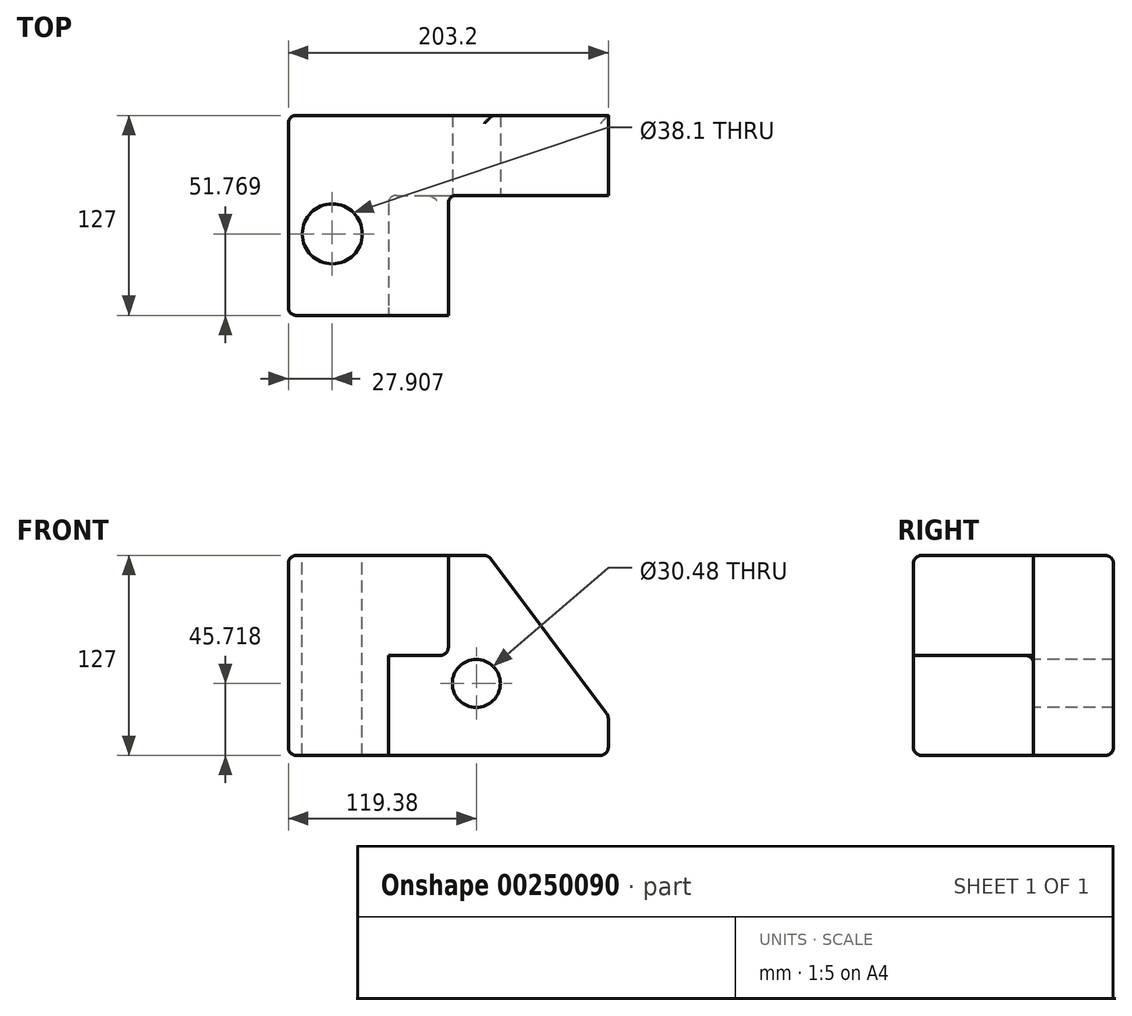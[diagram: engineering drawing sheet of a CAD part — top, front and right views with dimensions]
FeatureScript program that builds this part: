
annotation { "Feature Type Name" : "Feature", "Feature Type Description" : "" }
export const myFeature = defineFeature(function(context is Context, id is Id, definition is map)
    precondition{}
    {
        {
            var Q0;
            Q0=qCreatedBy(makeId("Front.planeOp"),FACE);
            var sketch = newSketch(context, id + "F0", { "sketchPlane" : qUnion([Q0])});
            skLineSegment(sketch, "E0.bottom", {"start": v(-90.02, 64.6) * mm, "end": v(113.18, 64.6) * mm});
            skLineSegment(sketch, "E0.top", {"start": v(-90.02, -62.4) * mm, "end": v(113.18, -62.4) * mm});
            skLineSegment(sketch, "E0.left", {"start": v(-90.02, 64.6) * mm, "end": v(-90.02, -62.4) * mm});
            skLineSegment(sketch, "E0.right", {"start": v(113.18, 64.6) * mm, "end": v(113.18, -62.4) * mm});
            skSolve(sketch);
        }
        {
            var Q0;
            Q0 = qSketchRegion(id + "F0", true);
            extrude(context, id + "F1", {"entities" : qUnion([Q0]), "depth" : 127 * mm});
        }
        {
            var Q0;
            Q0=makeQuery(id+"F1.opExtrude","CAP_FACE",FACE,{"disambiguationData":[OSD([sQuery(id+"F0.wireOp",EDGE,"E0.bottom"),sQuery(id+"F0.wireOp",EDGE,"E0.top"),sQuery(id+"F0.wireOp",EDGE,"E0.left"),sQuery(id+"F0.wireOp",EDGE,"E0.right")])],"isStart":false});
            var sketch = newSketch(context, id + "F2", { "sketchPlane" : qUnion([Q0])});
            skLineSegment(sketch, "E1.top", {"start": v(-90.02, -62.4) * mm, "end": v(-26.52, -62.4) * mm});
            skLineSegment(sketch, "E1.left", {"start": v(-90.02, 64.6) * mm, "end": v(-90.02, -62.4) * mm});
            skLineSegment(sketch, "E1.right", {"start": v(-26.52, 1.1) * mm, "end": v(-26.52, -62.4) * mm});
            skLineSegment(sketch, "E2", {"start": v(-26.52, 1.1) * mm, "end": v(11.58, 1.1) * mm});
            skLineSegment(sketch, "E3", {"start": v(11.58, 1.1) * mm, "end": v(11.58, 64.6) * mm});
            skLineSegment(sketch, "E4", {"start": v(-90.02, 64.6) * mm, "end": v(11.58, 64.6) * mm});
            skSolve(sketch);
        }
        {
            var Q0;
            {var subQ3=sQuery(id+"F2.wireOp",EDGE,"E1.right");Q0=makeQuery(id+"F2.imprint","IMPRINT",FACE,{"disambiguationData":[TD([[makeQuery(id+"F2.imprint","IMPRINT",EDGE,{"derivedFrom":subQ3}),1.0]])]});}
            extrude(context, id + "F3", {"entities" : qUnion([Q0]), "operationType" : NewBodyOperationType.REMOVE, "oppositeDirection" : true, "depth" : 76.2 * mm});
        }
        {
            var Q0;
            Q0=makeQuery(id+"F1.opExtrude","SWEPT_EDGE",EDGE,{"disambiguationData":[OSD([sQuery(id+"F0.wireOp",EDGE,"E0.bottom"),sQuery(id+"F0.wireOp",EDGE,"E0.right")])]});
            chamfer(context, id + "F4", {"entities" : qUnion([Q0]), "chamferType" : ChamferType.TWO_OFFSETS, "width1" : 76.2 * mm, "oppositeDirection" : false, "width2" : 101.6 * mm, "tangentPropagation" : true});
        }
        {
            var Q0;
            Q0=makeQuery(id+"F3.boolean.opBoolean","COPY",EDGE,{"derivedFrom":makeQuery(id+"F3.opExtrude","SWEPT_EDGE",EDGE,{"disambiguationData":[OSD([sQuery(id+"F0.wireOp",EDGE,"E0.bottom"),sQuery(id+"F2.wireOp",EDGE,"E3"),sQuery(id+"F2.wireOp",EDGE,"E4")])]})});
            var Q1;
            Q1=makeQuery(id+"F3.boolean.opBoolean","COPY",EDGE,{"derivedFrom":makeQuery(id+"F3.opExtrude","SWEPT_EDGE",EDGE,{"disambiguationData":[OSD([sQuery(id+"F2.wireOp",EDGE,"E2"),sQuery(id+"F2.wireOp",EDGE,"E3")])]})});
            var Q2;
            Q2=makeQuery(id+"F3.boolean.opBoolean","COPY",EDGE,{"derivedFrom":makeQuery(id+"F3.opExtrude","CAP_EDGE",EDGE,{"disambiguationData":[OSD([sQuery(id+"F2.wireOp",EDGE,"E3")])],"isStart":false})});
            var Q3;
            Q3=makeQuery(id+"F3.boolean.opBoolean","COPY",EDGE,{"derivedFrom":makeQuery(id+"F3.opExtrude","CAP_EDGE",EDGE,{"disambiguationData":[OSD([sQuery(id+"F2.wireOp",EDGE,"E1.right")])],"isStart":false})});
            var Q4;
            Q4=makeQuery(id+"F3.boolean.opBoolean","COPY",EDGE,{"derivedFrom":makeQuery(id+"F3.opExtrude","CAP_EDGE",EDGE,{"disambiguationData":[OSD([sQuery(id+"F2.wireOp",EDGE,"E1.right")])],"isStart":true})});
            var Q5;
            Q5=makeQuery(id+"F3.boolean.opBoolean","COPY",EDGE,{"derivedFrom":makeQuery(id+"F3.opExtrude","SWEPT_EDGE",EDGE,{"disambiguationData":[OSD([sQuery(id+"F0.wireOp",EDGE,"E0.top"),sQuery(id+"F2.wireOp",EDGE,"E1.top"),sQuery(id+"F2.wireOp",EDGE,"E1.right")])]})});
            var Q6;
            Q6=makeQuery(id+"F3.boolean.opBoolean","COPY",EDGE,{"derivedFrom":makeQuery(id+"F3.opExtrude","CAP_EDGE",EDGE,{"disambiguationData":[OSD([sQuery(id+"F2.wireOp",EDGE,"E2")])],"isStart":true})});
            var Q7;
            Q7=makeQuery(id+"F1.opExtrude","CAP_EDGE",EDGE,{"disambiguationData":[OSD([sQuery(id+"F0.wireOp",EDGE,"E0.bottom")])],"isStart":false});
            var Q8;
            Q8=makeQuery(id+"F1.opExtrude","SWEPT_EDGE",EDGE,{"disambiguationData":[OSD([sQuery(id+"F0.wireOp",EDGE,"E0.bottom"),sQuery(id+"F0.wireOp",EDGE,"E0.left")])]});
            var Q9;
            Q9=makeQuery(id+"F1.opExtrude","CAP_EDGE",EDGE,{"disambiguationData":[OSD([sQuery(id+"F0.wireOp",EDGE,"E0.bottom")])],"isStart":true});
            var Q10;
            Q10=makeQuery(id+"F1.opExtrude","CAP_EDGE",EDGE,{"disambiguationData":[OSD([sQuery(id+"F0.wireOp",EDGE,"E0.top")])],"isStart":false});
            var Q11;
            Q11=makeQuery(id+"F1.opExtrude","CAP_EDGE",EDGE,{"disambiguationData":[OSD([sQuery(id+"F0.wireOp",EDGE,"E0.left")])],"isStart":false});
            var Q12;
            Q12=makeQuery(id+"F3.boolean.opBoolean","COPY",EDGE,{"derivedFrom":makeQuery(id+"F3.opExtrude","CAP_EDGE",EDGE,{"disambiguationData":[OSD([sQuery(id+"F0.wireOp",EDGE,"E0.top")])],"isStart":false})});
            var Q13;
            Q13=makeQuery(id+"F1.opExtrude","SWEPT_EDGE",EDGE,{"disambiguationData":[OSD([sQuery(id+"F0.wireOp",EDGE,"E0.top"),sQuery(id+"F0.wireOp",EDGE,"E0.right")])]});
            var Q14;
            {var subQ0=sQuery(id+"F0.wireOp",EDGE,"E0.bottom");Q14=makeQuery(id+"F4.opChamfer","BLEND_EDGE",EDGE,{"blendedFrom":[makeQuery(id+"F1.opExtrude","SWEPT_EDGE",EDGE,{"disambiguationData":[OSD([subQ0,sQuery(id+"F0.wireOp",EDGE,"E0.right")])]}),makeQuery(id+"F1.opExtrude","SWEPT_FACE",FACE,{"disambiguationData":[OSD([subQ0])]})],"blendedInto":[makeQuery(id+"F1.opExtrude","SWEPT_FACE",FACE,{"disambiguationData":[OSD([subQ0])]})]});}
            var Q15;
            {var subQ0=sQuery(id+"F0.wireOp",EDGE,"E0.right");Q15=makeQuery(id+"F4.opChamfer","BLEND_EDGE",EDGE,{"blendedFrom":[makeQuery(id+"F1.opExtrude","SWEPT_EDGE",EDGE,{"disambiguationData":[OSD([sQuery(id+"F0.wireOp",EDGE,"E0.bottom"),subQ0])]}),makeQuery(id+"F1.opExtrude","SWEPT_FACE",FACE,{"disambiguationData":[OSD([subQ0])]})],"blendedInto":[makeQuery(id+"F1.opExtrude","SWEPT_FACE",FACE,{"disambiguationData":[OSD([subQ0])]})]});}
            var Q16;
            Q16=makeQuery(id+"F1.opExtrude","CAP_EDGE",EDGE,{"disambiguationData":[OSD([sQuery(id+"F0.wireOp",EDGE,"E0.top")])],"isStart":true});
            var Q17;
            Q17=makeQuery(id+"F1.opExtrude","CAP_EDGE",EDGE,{"disambiguationData":[OSD([sQuery(id+"F0.wireOp",EDGE,"E0.left")])],"isStart":true});
            var Q18;
            Q18=makeQuery(id+"F1.opExtrude","SWEPT_EDGE",EDGE,{"disambiguationData":[OSD([sQuery(id+"F0.wireOp",EDGE,"E0.top"),sQuery(id+"F0.wireOp",EDGE,"E0.left")])]});
            fillet(context, id + "F5", {"entities" : qUnion([Q0, Q1, Q2, Q3, Q4, Q5, Q6, Q7, Q8, Q9, Q10, Q11, Q12, Q13, Q14, Q15, Q16, Q17, Q18]), "radius" : 5.08 * mm, "tangentPropagation" : true, "allowEdgeOverflow" : false});
        }
        {
            var Q0;
            Q0=makeQuery(id+"F3.boolean.opBoolean","COPY",FACE,{"derivedFrom":makeQuery(id+"F3.opExtrude","CAP_FACE",FACE,{"disambiguationData":[OSD([sQuery(id+"F0.wireOp",EDGE,"E0.bottom"),sQuery(id+"F0.wireOp",EDGE,"E0.top"),sQuery(id+"F0.wireOp",EDGE,"E0.right"),sQuery(id+"F2.wireOp",EDGE,"E1.right"),sQuery(id+"F2.wireOp",EDGE,"E2"),sQuery(id+"F2.wireOp",EDGE,"E3")])],"isStart":false})});
            var sketch = newSketch(context, id + "F6", { "sketchPlane" : qUnion([Q0])});
            skCircle(sketch, "E5", {"center": v(29.36, -16.67) * mm, "radius": 15.24 * mm});
            skSolve(sketch);
        }
        {
            var Q0;
            Q0 = qSketchRegion(id + "F6", true);
            var Q1;
            Q1=makeQuery(id+"F1.opExtrude","CAP_FACE",FACE,{"disambiguationData":[OSD([sQuery(id+"F0.wireOp",EDGE,"E0.bottom"),sQuery(id+"F0.wireOp",EDGE,"E0.top"),sQuery(id+"F0.wireOp",EDGE,"E0.left"),sQuery(id+"F0.wireOp",EDGE,"E0.right")])],"isStart":true});
            extrude(context, id + "F7", {"entities" : qUnion([Q0]), "operationType" : NewBodyOperationType.REMOVE, "endBound" : BoundingType.UP_TO_SURFACE, "oppositeDirection" : true, "endBoundEntityFace" : qUnion([Q1]), "depth" : 25.4 * mm});
        }
        {
            var Q0;
            Q0=makeQuery(id+"F1.opExtrude","SWEPT_FACE",FACE,{"disambiguationData":[OSD([sQuery(id+"F0.wireOp",EDGE,"E0.bottom")])]});
            var sketch = newSketch(context, id + "F8", { "sketchPlane" : qUnion([Q0])});
            skCircle(sketch, "E6", {"center": v(-62.11, -75.23) * mm, "radius": 19.05 * mm});
            skSolve(sketch);
        }
        {
            var Q0;
            Q0=makeQuery(id+"F8.imprint","IMPRINT",FACE,{"disambiguationData":[TD([[makeQuery(id+"F8.imprint","IMPRINT",EDGE,{"derivedFrom":sQuery(id+"F8.wireOp",EDGE,"E6")}),1.0]])]});
            extrude(context, id + "F9", {"entities" : qUnion([Q0]), "operationType" : NewBodyOperationType.REMOVE, "oppositeDirection" : true, "depth" : 127 * mm});
        }
    });
